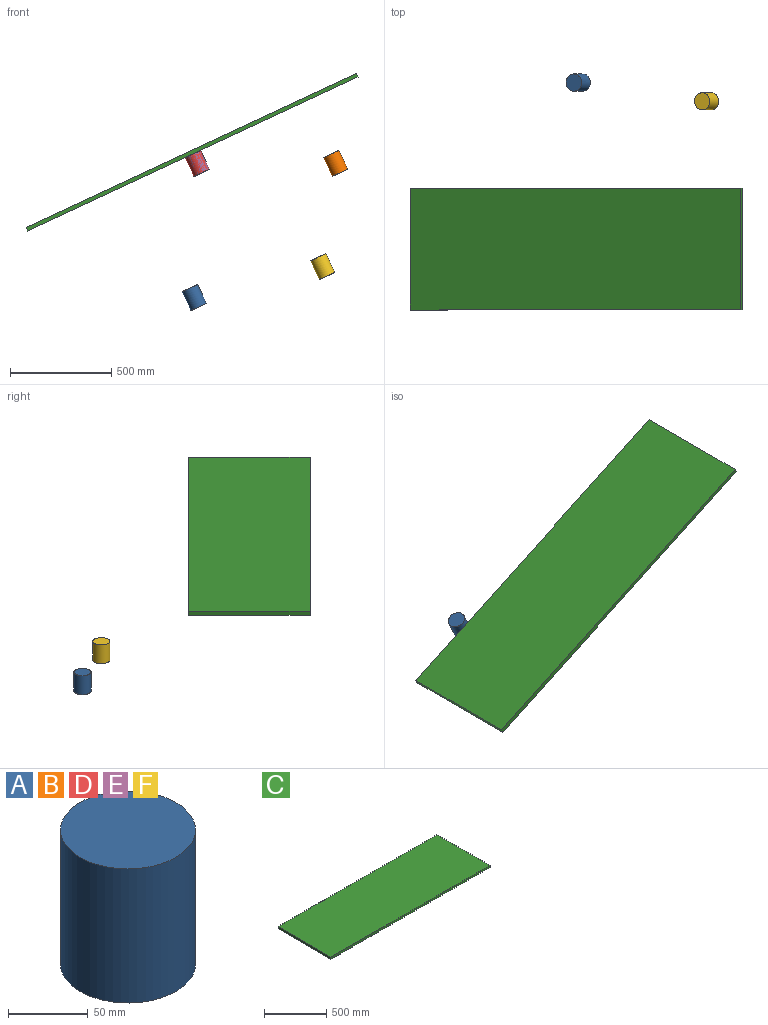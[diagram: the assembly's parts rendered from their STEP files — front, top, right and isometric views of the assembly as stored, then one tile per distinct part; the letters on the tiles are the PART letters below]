
ASSEMBLY  parts=6 mates=2
PART A: 3 faces, bbox 84.7x84.7x103 mm
  f0: cylinder r=42.36mm len=103mm, axis (0,0,1), area 27413.8mm2, adj f1,f2
  f1: plane 84.72x84.72mm, normal (0,0,-1), area 5637.1mm2, adj f0
  f2: plane 84.72x84.72mm, normal (0,0,1), area 5637.1mm2, adj f0
PART B: same geometry as A
PART C: 6 faces, bbox 1800x600x20 mm
  f0: plane 1800x20mm, normal (0,1,0), area 36000mm2, adj f1,f3,f4,f5
  f1: plane 600x20mm, normal (-1,0,0), area 12000mm2, adj f0,f2,f4,f5
  f2: plane 1800x20mm, normal (0,-1,0), area 36000mm2, adj f1,f3,f4,f5
  f3: plane 600x20mm, normal (1,0,0), area 12000mm2, adj f0,f2,f4,f5
  f4: plane 1800x600mm, normal (0,0,1), area 1080000mm2, adj f0,f1,f2,f3
  f5: plane 1800x600mm, normal (0,0,-1), area 1080000mm2, adj f0,f1,f2,f3
PART D: same geometry as A
PART E: same geometry as A
PART F: same geometry as A
PLACE A rot(axis=(0,-1,0),25deg) t=(-1145.23,372.15,-398.5)mm
PLACE B rot(axis=(0,-1,0),25deg) t=(-446.98,-316.49,263.9)mm
PLACE C rot(axis=(0,-1,0),25deg) t=(-1130.32,-451.94,263.65)mm
PLACE D rot(axis=(0,-1,0),25deg) t=(-1130.32,-451.94,263.65)mm
PLACE E rot(axis=(0,-1,0),25deg) t=(-1130.32,-451.94,263.65)mm
PLACE F rot(axis=(0,-1,0),25deg) t=(-511.49,279.03,-246.02)mm
MATE fastened C.f5 <-> D.f0  axis (0.42,0,-0.91) through (-1130.32,-451.94,263.65)mm
MATE fastened C.f5 <-> E.f0  axis (0.42,0,-0.91) through (-1130.32,-451.94,263.65)mm
